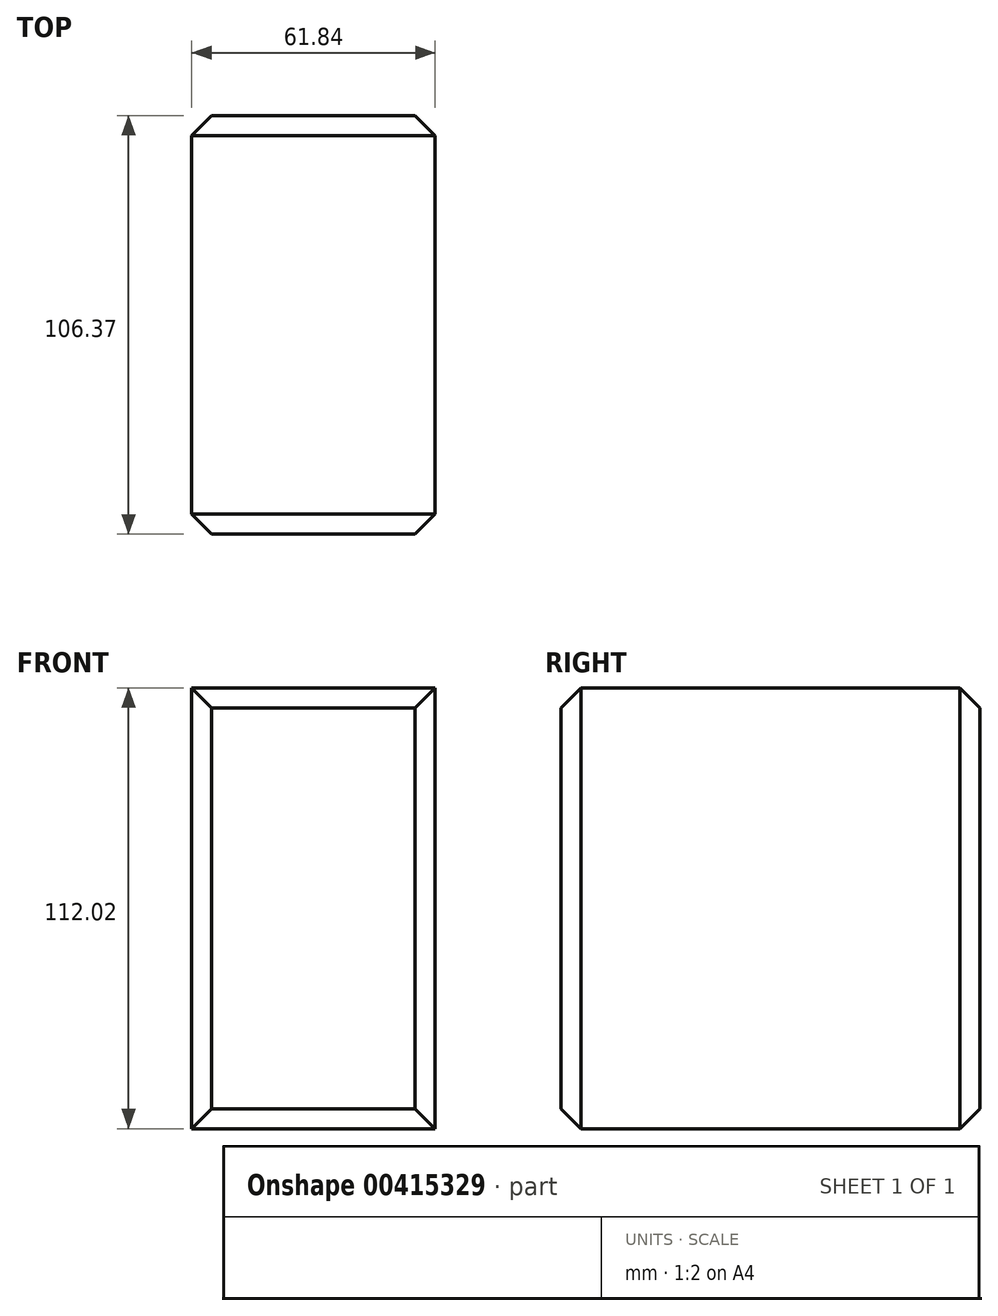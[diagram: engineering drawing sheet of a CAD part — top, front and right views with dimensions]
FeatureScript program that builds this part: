
annotation { "Feature Type Name" : "Feature", "Feature Type Description" : "" }
export const myFeature = defineFeature(function(context is Context, id is Id, definition is map)
    precondition{}
    {
        {
            var Q0;
            Q0=qCreatedBy(makeId("Top.planeOp"),FACE);
            var sketch = newSketch(context, id + "F0", { "sketchPlane" : qUnion([Q0])});
            skLineSegment(sketch, "E0.bottom", {"start": v(0, 74.65) * mm, "end": v(61.84, 74.65) * mm});
            skLineSegment(sketch, "E0.top", {"start": v(0, -31.72) * mm, "end": v(61.84, -31.72) * mm});
            skLineSegment(sketch, "E0.left", {"start": v(0, 74.65) * mm, "end": v(0, -31.72) * mm});
            skLineSegment(sketch, "E0.right", {"start": v(61.84, 74.65) * mm, "end": v(61.84, -31.72) * mm});
            skSolve(sketch);
        }
        {
            var Q0;
            Q0 = qSketchRegion(id + "F0", true);
            extrude(context, id + "F1", {"entities" : qUnion([Q0]), "depth" : 112.02 * mm});
        }
        {
            var Q0;
            Q0=makeQuery(id+"F1.opExtrude","SWEPT_FACE",FACE,{"disambiguationData":[OSD([sQuery(id+"F0.wireOp",EDGE,"E0.top")])]});
            chamfer(context, id + "F2", {"entities" : qUnion([Q0]), "width" : 5.08 * mm, "tangentPropagation" : true});
        }
        {
            var Q0;
            Q0=makeQuery(id+"F1.opExtrude","SWEPT_FACE",FACE,{"disambiguationData":[OSD([sQuery(id+"F0.wireOp",EDGE,"E0.bottom")])]});
            chamfer(context, id + "F3", {"entities" : qUnion([Q0]), "width" : 5.08 * mm, "tangentPropagation" : true});
        }
    });
